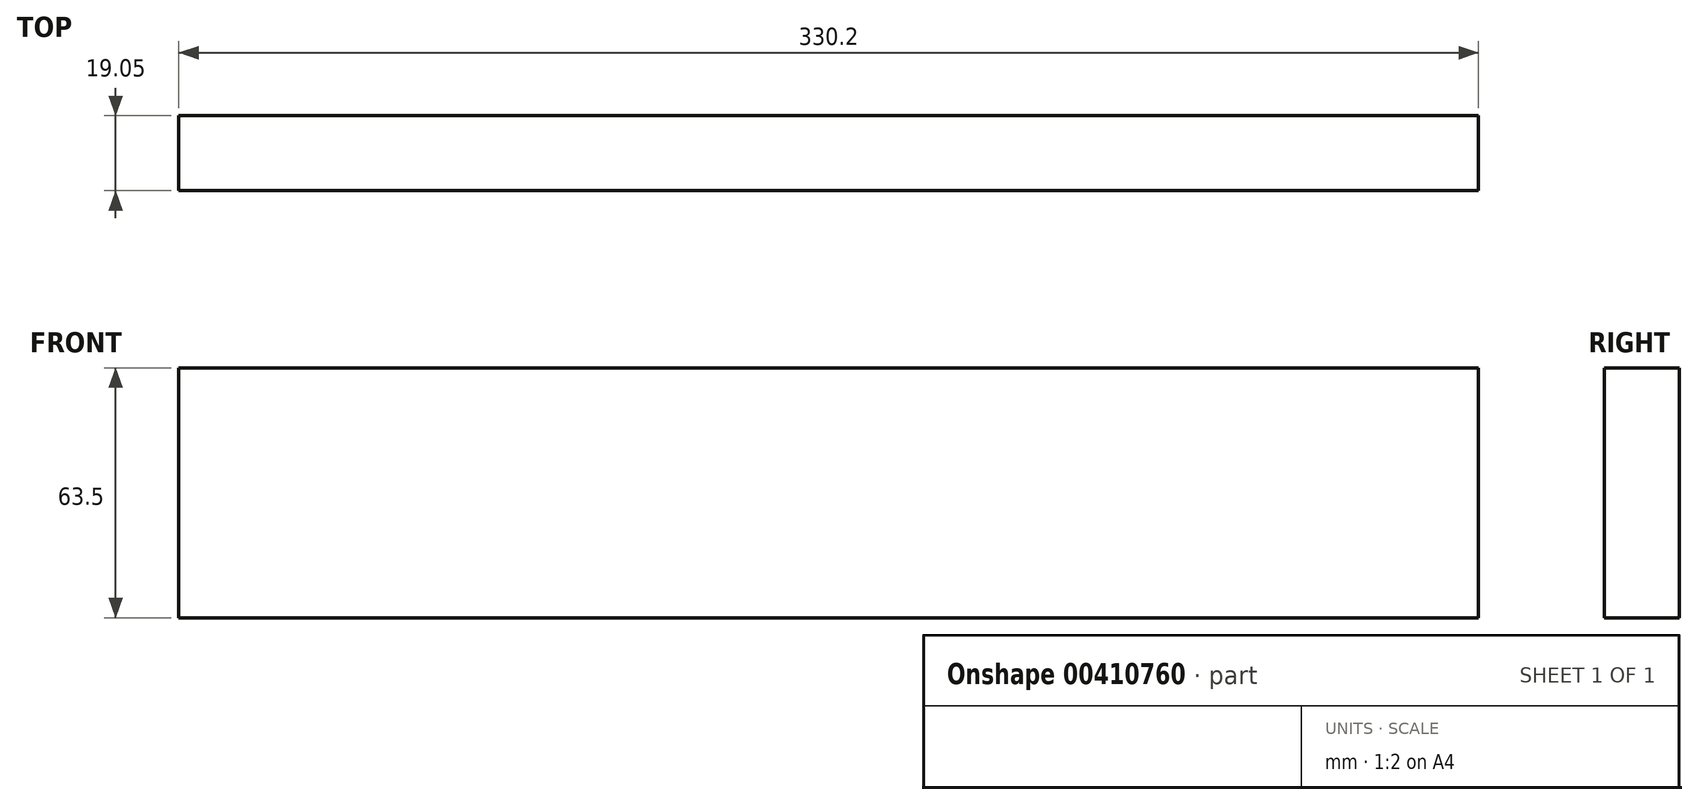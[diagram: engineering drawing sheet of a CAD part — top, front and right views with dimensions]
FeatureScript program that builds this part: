
annotation { "Feature Type Name" : "Feature", "Feature Type Description" : "" }
export const myFeature = defineFeature(function(context is Context, id is Id, definition is map)
    precondition{}
    {
        {
            var Q0;
            Q0=qCreatedBy(makeId("Front.planeOp"),FACE);
            var sketch = newSketch(context, id + "F0", { "sketchPlane" : qUnion([Q0])});
            skLineSegment(sketch, "E0.bottom", {"start": v(0, 0) * mm, "end": v(330.2, 0) * mm});
            skLineSegment(sketch, "E0.top", {"start": v(0, 63.5) * mm, "end": v(330.2, 63.5) * mm});
            skLineSegment(sketch, "E0.left", {"start": v(0, 0) * mm, "end": v(0, 63.5) * mm});
            skLineSegment(sketch, "E0.right", {"start": v(330.2, 0) * mm, "end": v(330.2, 63.5) * mm});
            skSolve(sketch);
        }
        {
            var Q0;
            Q0 = qSketchRegion(id + "F0", true);
            extrude(context, id + "F1", {"entities" : qUnion([Q0]), "depth" : 19.05 * mm});
        }
    });
